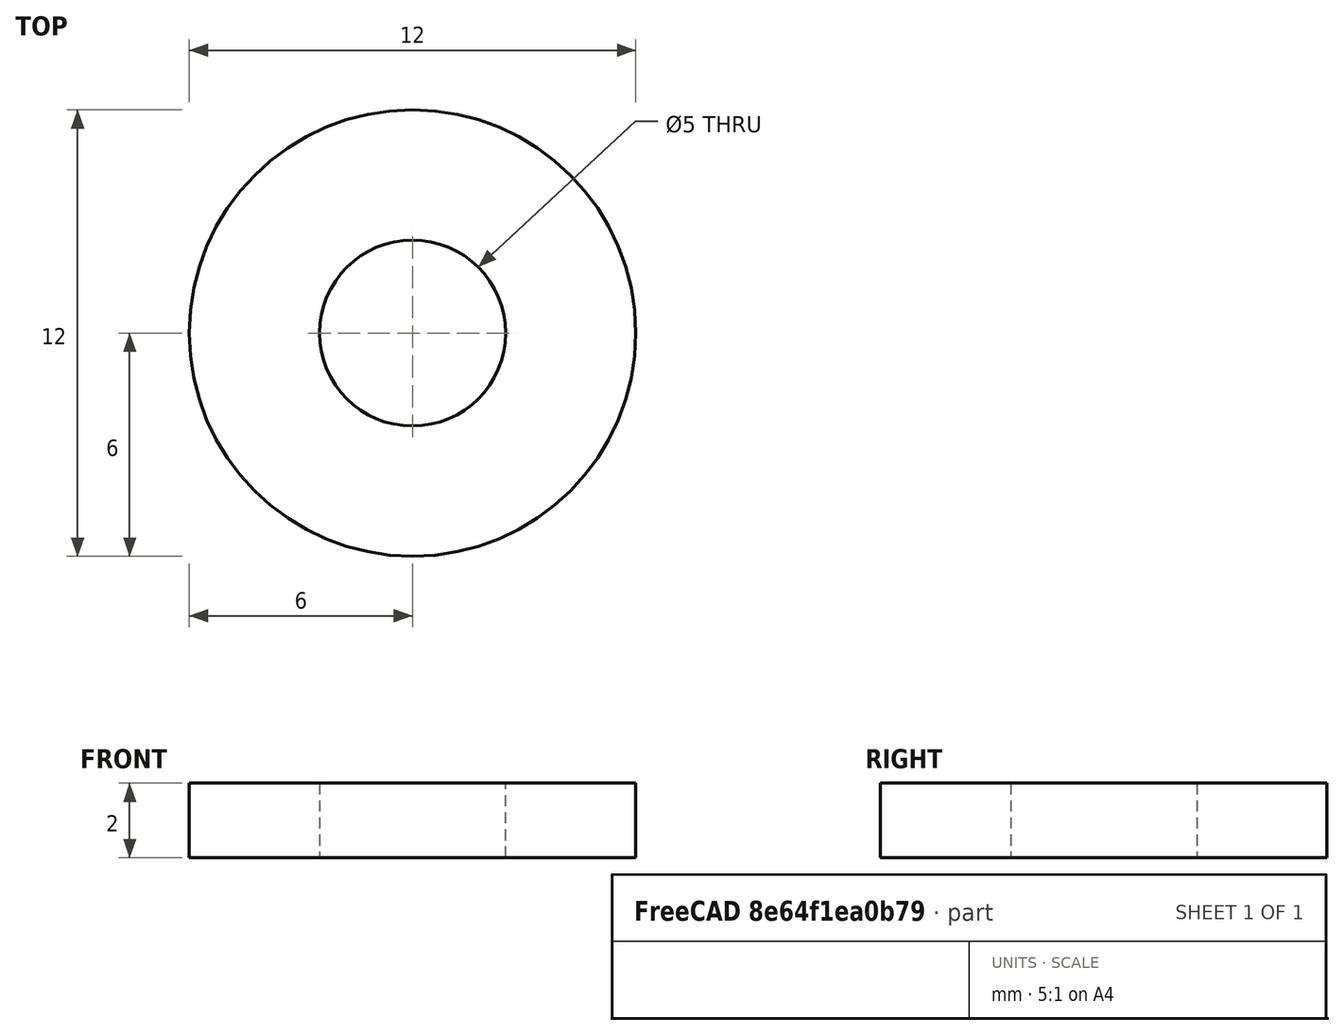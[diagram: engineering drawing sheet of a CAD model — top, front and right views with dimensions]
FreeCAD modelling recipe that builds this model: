
FCSTD DOCUMENT  (FreeCAD 0.19R24276 (Git))
Label: Rolik_1__part_2_print
License: All rights reserved
LicenseURL: http://en.wikipedia.org/wiki/All_rights_reserved
objects: Sketcher::SketchObject×1, PartDesign::Pad×1, PartDesign::Body×1
note: 4 computed .brp shape members not serialized (recipe doc carries the construction recipe); baked Part::Feature solids carry a one-line shape summary decoded from their .brp

FEATURE [Sketcher::SketchObject] Sketch
  FullyConstrained = true
  MapMode = 5
  Support = -> [XY_Plane]
  sketch-geometry (2):
    g0: Circle CenterX=0 CenterY=0 CenterZ=0 NormalX=0 NormalY=0 NormalZ=1 AngleXU=0 Radius=2.5
    g1: Circle CenterX=0 CenterY=0 CenterZ=0 NormalX=0 NormalY=0 NormalZ=1 AngleXU=0 Radius=6
  constraints (4):
    c: Coincident(g0,g-1)
    c: Coincident(g1,g0)
    c: Diameter(g0) = 5
    c: Diameter(g1) = 12
FEATURE [PartDesign::Pad] Pad
  Direction = (1,1,1)
  Length = 2
  Length2 = 100
  Profile = -> Sketch
  Type = 0
FEATURE [PartDesign::Body] Body
  Group = -> [Sketch,Pad]
  Origin = -> Origin
  Tip = -> Pad
